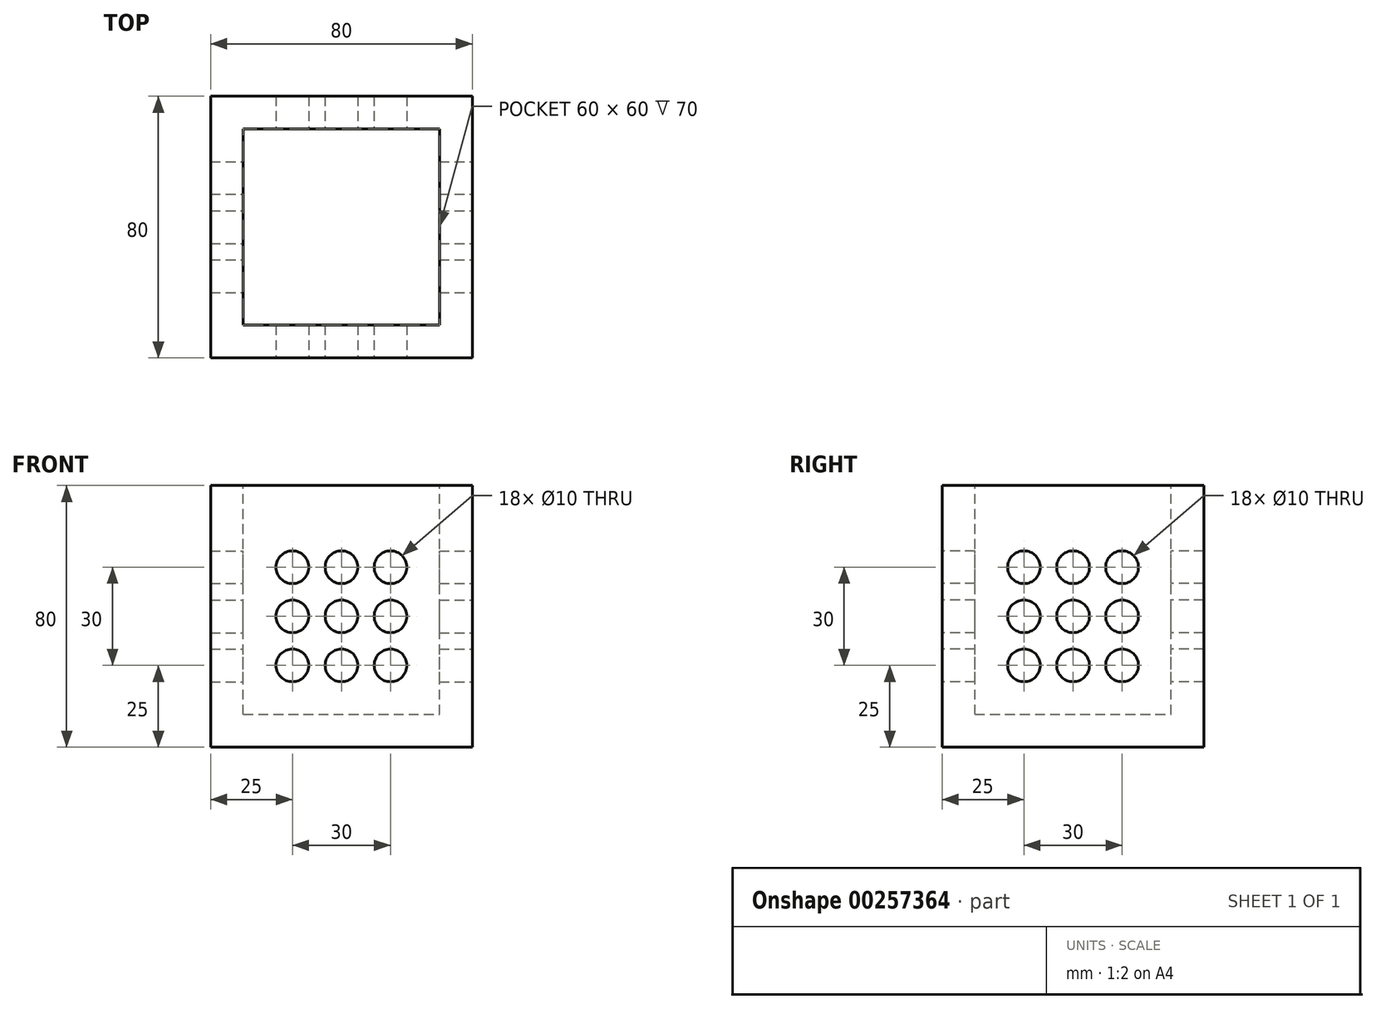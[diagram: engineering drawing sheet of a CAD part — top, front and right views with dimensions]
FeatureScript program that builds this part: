
annotation { "Feature Type Name" : "Feature", "Feature Type Description" : "" }
export const myFeature = defineFeature(function(context is Context, id is Id, definition is map)
    precondition{}
    {
        {
            var Q0;
            Q0=qCreatedBy(makeId("Front.planeOp"),FACE);
            var sketch = newSketch(context, id + "F0", { "sketchPlane" : qUnion([Q0])});
            skLineSegment(sketch, "E0.bottom", {"start": v(0, 0) * mm, "end": v(80, 0) * mm});
            skLineSegment(sketch, "E0.top", {"start": v(0, 80) * mm, "end": v(80, 80) * mm});
            skLineSegment(sketch, "E0.left", {"start": v(0, 0) * mm, "end": v(0, 80) * mm});
            skLineSegment(sketch, "E0.right", {"start": v(80, 0) * mm, "end": v(80, 80) * mm});
            skSolve(sketch);
        }
        {
            var Q0;
            Q0=makeQuery(id+"F0.imprint","IMPRINT",FACE,{"disambiguationData":[TD([[makeQuery(id+"F0.imprint","IMPRINT",EDGE,{"derivedFrom":sQuery(id+"F0.wireOp",EDGE,"E0.bottom")}),1.0]])]});
            extrude(context, id + "F1", {"entities" : qUnion([Q0]), "depth" : 80 * mm});
        }
        {
            var Q0;
            Q0=makeQuery(id+"F1.opExtrude","SWEPT_FACE",FACE,{"disambiguationData":[OSD([sQuery(id+"F0.wireOp",EDGE,"E0.top")])]});
            var sketch = newSketch(context, id + "F2", { "sketchPlane" : qUnion([Q0])});
            skLineSegment(sketch, "E1.bottom", {"start": v(10, -70) * mm, "end": v(70, -70) * mm});
            skLineSegment(sketch, "E1.top", {"start": v(10, -10) * mm, "end": v(70, -10) * mm});
            skLineSegment(sketch, "E1.left", {"start": v(10, -70) * mm, "end": v(10, -10) * mm});
            skLineSegment(sketch, "E1.right", {"start": v(70, -70) * mm, "end": v(70, -10) * mm});
            skSolve(sketch);
        }
        {
            var Q0;
            Q0=makeQuery(id+"F2.imprint","IMPRINT",FACE,{"disambiguationData":[TD([[makeQuery(id+"F2.imprint","IMPRINT",EDGE,{"derivedFrom":sQuery(id+"F2.wireOp",EDGE,"E1.bottom")}),1.0]])]});
            extrude(context, id + "F3", {"entities" : qUnion([Q0]), "operationType" : NewBodyOperationType.REMOVE, "oppositeDirection" : true, "depth" : 70 * mm});
        }
        {
            var Q0;
            Q0=makeQuery(id+"F1.opExtrude","CAP_FACE",FACE,{"disambiguationData":[OSD([sQuery(id+"F0.wireOp",EDGE,"E0.bottom"),sQuery(id+"F0.wireOp",EDGE,"E0.top"),sQuery(id+"F0.wireOp",EDGE,"E0.left"),sQuery(id+"F0.wireOp",EDGE,"E0.right")])],"isStart":false});
            var sketch = newSketch(context, id + "F4", { "sketchPlane" : qUnion([Q0])});
            skLineSegment(sketch, "E2.bottom", {"start": v(10, 10) * mm, "end": v(70, 10) * mm});
            skLineSegment(sketch, "E2.top", {"start": v(10, 70) * mm, "end": v(70, 70) * mm});
            skLineSegment(sketch, "E2.left", {"start": v(10, 10) * mm, "end": v(10, 70) * mm});
            skLineSegment(sketch, "E2.right", {"start": v(70, 10) * mm, "end": v(70, 70) * mm});
            skLineSegment(sketch, "E3", {"start": v(25, 10) * mm, "end": v(25, 20) * mm});
            skLineSegment(sketch, "E4", {"start": v(40, 10) * mm, "end": v(40, 20) * mm});
            skLineSegment(sketch, "E5", {"start": v(55, 10) * mm, "end": v(55, 20) * mm});
            skLineSegment(sketch, "E6", {"start": v(10, 55) * mm, "end": v(20, 55) * mm});
            skLineSegment(sketch, "E7", {"start": v(10, 40) * mm, "end": v(20, 40) * mm});
            skLineSegment(sketch, "E8", {"start": v(10, 25) * mm, "end": v(20, 25) * mm});
            skCircle(sketch, "E9", {"center": v(25, 55) * mm, "radius": 5 * mm});
            skCircle(sketch, "E10", {"center": v(40, 55) * mm, "radius": 5 * mm});
            skCircle(sketch, "E11", {"center": v(55, 55) * mm, "radius": 5 * mm});
            skCircle(sketch, "E12", {"center": v(55, 40) * mm, "radius": 5 * mm});
            skCircle(sketch, "E13", {"center": v(40, 40) * mm, "radius": 5 * mm});
            skCircle(sketch, "E14", {"center": v(25, 40) * mm, "radius": 5 * mm});
            skCircle(sketch, "E15", {"center": v(25, 25) * mm, "radius": 5 * mm});
            skCircle(sketch, "E16", {"center": v(40, 25) * mm, "radius": 5 * mm});
            skCircle(sketch, "E17", {"center": v(55, 25) * mm, "radius": 5 * mm});
            skLineSegment(sketch, "E18.trimOffspring", {"start": v(25, 60) * mm, "end": v(25, 70) * mm});
            skLineSegment(sketch, "E19.trimOffspring", {"start": v(30, 55) * mm, "end": v(35, 55) * mm});
            skLineSegment(sketch, "E20.trimOffspring", {"start": v(45, 55) * mm, "end": v(50, 55) * mm});
            skLineSegment(sketch, "E21.trimOffspring", {"start": v(40, 60) * mm, "end": v(40, 70) * mm});
            skLineSegment(sketch, "E22.trimOffspring", {"start": v(60, 55) * mm, "end": v(70, 55) * mm});
            skLineSegment(sketch, "E23.trimOffspring", {"start": v(55, 60) * mm, "end": v(55, 70) * mm});
            skLineSegment(sketch, "E24.trimOffspring", {"start": v(25, 45) * mm, "end": v(25, 50) * mm});
            skLineSegment(sketch, "E25.trimOffspring", {"start": v(30, 40) * mm, "end": v(35, 40) * mm});
            skLineSegment(sketch, "E26.trimOffspring", {"start": v(45, 40) * mm, "end": v(50, 40) * mm});
            skLineSegment(sketch, "E27.trimOffspring", {"start": v(40, 45) * mm, "end": v(40, 50) * mm});
            skLineSegment(sketch, "E28.trimOffspring", {"start": v(60, 40) * mm, "end": v(70, 40) * mm});
            skLineSegment(sketch, "E29.trimOffspring", {"start": v(55, 45) * mm, "end": v(55, 50) * mm});
            skLineSegment(sketch, "E30.trimOffspring", {"start": v(25, 30) * mm, "end": v(25, 35) * mm});
            skLineSegment(sketch, "E31.trimOffspring", {"start": v(30, 25) * mm, "end": v(35, 25) * mm});
            skLineSegment(sketch, "E32.trimOffspring", {"start": v(45, 25) * mm, "end": v(50, 25) * mm});
            skLineSegment(sketch, "E33.trimOffspring", {"start": v(40, 30) * mm, "end": v(40, 35) * mm});
            skLineSegment(sketch, "E34.trimOffspring", {"start": v(60, 25) * mm, "end": v(70, 25) * mm});
            skLineSegment(sketch, "E35.trimOffspring", {"start": v(55, 30) * mm, "end": v(55, 35) * mm});
            skSolve(sketch);
        }
        {
            var Q0;
            Q0=makeQuery(id+"F1.opExtrude","SWEPT_FACE",FACE,{"disambiguationData":[OSD([sQuery(id+"F0.wireOp",EDGE,"E0.right")])]});
            var sketch = newSketch(context, id + "F5", { "sketchPlane" : qUnion([Q0])});
            skLineSegment(sketch, "E36.bottom", {"start": v(-70, 10) * mm, "end": v(-10, 10) * mm});
            skLineSegment(sketch, "E36.top", {"start": v(-70, 70) * mm, "end": v(-10, 70) * mm});
            skLineSegment(sketch, "E36.left", {"start": v(-70, 10) * mm, "end": v(-70, 70) * mm});
            skLineSegment(sketch, "E36.right", {"start": v(-10, 10) * mm, "end": v(-10, 70) * mm});
            skLineSegment(sketch, "E37", {"start": v(-55, 10) * mm, "end": v(-55, 20) * mm});
            skLineSegment(sketch, "E38", {"start": v(-40, 10) * mm, "end": v(-40, 20) * mm});
            skLineSegment(sketch, "E39", {"start": v(-25, 10) * mm, "end": v(-25, 20) * mm});
            skLineSegment(sketch, "E40", {"start": v(-70, 55) * mm, "end": v(-60, 55) * mm});
            skLineSegment(sketch, "E41", {"start": v(-70, 40) * mm, "end": v(-60, 40) * mm});
            skLineSegment(sketch, "E42", {"start": v(-70, 25) * mm, "end": v(-60, 25) * mm});
            skCircle(sketch, "E43", {"center": v(-55, 55) * mm, "radius": 5 * mm});
            skCircle(sketch, "E44", {"center": v(-40, 55) * mm, "radius": 5 * mm});
            skCircle(sketch, "E45", {"center": v(-25, 55) * mm, "radius": 5 * mm});
            skCircle(sketch, "E46", {"center": v(-25, 40) * mm, "radius": 5 * mm});
            skCircle(sketch, "E47", {"center": v(-40, 40) * mm, "radius": 5 * mm});
            skCircle(sketch, "E48", {"center": v(-55, 40) * mm, "radius": 5 * mm});
            skCircle(sketch, "E49", {"center": v(-55, 25) * mm, "radius": 5 * mm});
            skCircle(sketch, "E50", {"center": v(-40, 25) * mm, "radius": 5 * mm});
            skCircle(sketch, "E51", {"center": v(-25, 25) * mm, "radius": 5 * mm});
            skLineSegment(sketch, "E52.trimOffspring", {"start": v(-55, 60) * mm, "end": v(-55, 70) * mm});
            skLineSegment(sketch, "E53.trimOffspring", {"start": v(-50, 55) * mm, "end": v(-45, 55) * mm});
            skLineSegment(sketch, "E54.trimOffspring", {"start": v(-35, 55) * mm, "end": v(-30, 55) * mm});
            skLineSegment(sketch, "E55.trimOffspring", {"start": v(-40, 60) * mm, "end": v(-40, 70) * mm});
            skLineSegment(sketch, "E56.trimOffspring", {"start": v(-20, 55) * mm, "end": v(-10, 55) * mm});
            skLineSegment(sketch, "E57.trimOffspring", {"start": v(-25, 60) * mm, "end": v(-25, 70) * mm});
            skLineSegment(sketch, "E58.trimOffspring", {"start": v(-55, 45) * mm, "end": v(-55, 50) * mm});
            skLineSegment(sketch, "E59.trimOffspring", {"start": v(-50, 40) * mm, "end": v(-45, 40) * mm});
            skLineSegment(sketch, "E60.trimOffspring", {"start": v(-35, 40) * mm, "end": v(-30, 40) * mm});
            skLineSegment(sketch, "E61.trimOffspring", {"start": v(-40, 45) * mm, "end": v(-40, 50) * mm});
            skLineSegment(sketch, "E62.trimOffspring", {"start": v(-20, 40) * mm, "end": v(-10, 40) * mm});
            skLineSegment(sketch, "E63.trimOffspring", {"start": v(-25, 45) * mm, "end": v(-25, 50) * mm});
            skLineSegment(sketch, "E64.trimOffspring", {"start": v(-55, 30) * mm, "end": v(-55, 35) * mm});
            skLineSegment(sketch, "E65.trimOffspring", {"start": v(-50, 25) * mm, "end": v(-45, 25) * mm});
            skLineSegment(sketch, "E66.trimOffspring", {"start": v(-35, 25) * mm, "end": v(-30, 25) * mm});
            skLineSegment(sketch, "E67.trimOffspring", {"start": v(-40, 30) * mm, "end": v(-40, 35) * mm});
            skLineSegment(sketch, "E68.trimOffspring", {"start": v(-20, 25) * mm, "end": v(-10, 25) * mm});
            skLineSegment(sketch, "E69.trimOffspring", {"start": v(-25, 30) * mm, "end": v(-25, 35) * mm});
            skSolve(sketch);
        }
        {
            var Q0;
            {var subQ0=sQuery(id+"F4.wireOp",EDGE,"E9");var subQ1=makeQuery(id+"F4.imprint","INTERSECT",VERTEX,{"derivedFrom":[subQ0,sQuery(id+"F4.wireOp",EDGE,"E18.trimOffspring")]});Q0=makeQuery(id+"F4.imprint","IMPRINT",FACE,{"disambiguationData":[TD([[makeQuery(id+"F4.imprint","IMPRINT",EDGE,{"disambiguationData":[TD([[subQ1,1.0]])],"derivedFrom":subQ0}),1.0]])]});}
            var Q1;
            {var subQ0=sQuery(id+"F4.wireOp",EDGE,"E10");var subQ1=makeQuery(id+"F4.imprint","INTERSECT",VERTEX,{"derivedFrom":[subQ0,sQuery(id+"F4.wireOp",EDGE,"E20.trimOffspring")]});Q1=makeQuery(id+"F4.imprint","IMPRINT",FACE,{"disambiguationData":[TD([[makeQuery(id+"F4.imprint","IMPRINT",EDGE,{"disambiguationData":[TD([[subQ1,-1.0]])],"derivedFrom":subQ0}),1.0]])]});}
            var Q2;
            {var subQ0=sQuery(id+"F4.wireOp",EDGE,"E11");var subQ1=makeQuery(id+"F4.imprint","INTERSECT",VERTEX,{"derivedFrom":[subQ0,sQuery(id+"F4.wireOp",EDGE,"E22.trimOffspring")]});Q2=makeQuery(id+"F4.imprint","IMPRINT",FACE,{"disambiguationData":[TD([[makeQuery(id+"F4.imprint","IMPRINT",EDGE,{"disambiguationData":[TD([[subQ1,-1.0]])],"derivedFrom":subQ0}),1.0]])]});}
            var Q3;
            {var subQ0=sQuery(id+"F4.wireOp",EDGE,"E12");var subQ1=makeQuery(id+"F4.imprint","INTERSECT",VERTEX,{"derivedFrom":[subQ0,sQuery(id+"F4.wireOp",EDGE,"E28.trimOffspring")]});Q3=makeQuery(id+"F4.imprint","IMPRINT",FACE,{"disambiguationData":[TD([[makeQuery(id+"F4.imprint","IMPRINT",EDGE,{"disambiguationData":[TD([[subQ1,-1.0]])],"derivedFrom":subQ0}),1.0]])]});}
            var Q4;
            {var subQ0=sQuery(id+"F4.wireOp",EDGE,"E17");var subQ1=makeQuery(id+"F4.imprint","INTERSECT",VERTEX,{"derivedFrom":[subQ0,sQuery(id+"F4.wireOp",EDGE,"E34.trimOffspring")]});Q4=makeQuery(id+"F4.imprint","IMPRINT",FACE,{"disambiguationData":[TD([[makeQuery(id+"F4.imprint","IMPRINT",EDGE,{"disambiguationData":[TD([[subQ1,-1.0]])],"derivedFrom":subQ0}),1.0]])]});}
            var Q5;
            {var subQ0=sQuery(id+"F4.wireOp",EDGE,"E16");var subQ1=makeQuery(id+"F4.imprint","INTERSECT",VERTEX,{"derivedFrom":[subQ0,sQuery(id+"F4.wireOp",EDGE,"E32.trimOffspring")]});Q5=makeQuery(id+"F4.imprint","IMPRINT",FACE,{"disambiguationData":[TD([[makeQuery(id+"F4.imprint","IMPRINT",EDGE,{"disambiguationData":[TD([[subQ1,-1.0]])],"derivedFrom":subQ0}),1.0]])]});}
            var Q6;
            {var subQ0=sQuery(id+"F4.wireOp",EDGE,"E13");var subQ1=makeQuery(id+"F4.imprint","INTERSECT",VERTEX,{"derivedFrom":[subQ0,sQuery(id+"F4.wireOp",EDGE,"E26.trimOffspring")]});Q6=makeQuery(id+"F4.imprint","IMPRINT",FACE,{"disambiguationData":[TD([[makeQuery(id+"F4.imprint","IMPRINT",EDGE,{"disambiguationData":[TD([[subQ1,-1.0]])],"derivedFrom":subQ0}),1.0]])]});}
            var Q7;
            {var subQ0=sQuery(id+"F4.wireOp",EDGE,"E14");var subQ1=makeQuery(id+"F4.imprint","INTERSECT",VERTEX,{"derivedFrom":[subQ0,sQuery(id+"F4.wireOp",EDGE,"E24.trimOffspring")]});Q7=makeQuery(id+"F4.imprint","IMPRINT",FACE,{"disambiguationData":[TD([[makeQuery(id+"F4.imprint","IMPRINT",EDGE,{"disambiguationData":[TD([[subQ1,1.0]])],"derivedFrom":subQ0}),1.0]])]});}
            var Q8;
            {var subQ0=sQuery(id+"F4.wireOp",EDGE,"E15");var subQ1=makeQuery(id+"F4.imprint","INTERSECT",VERTEX,{"derivedFrom":[subQ0,sQuery(id+"F4.wireOp",EDGE,"E30.trimOffspring")]});Q8=makeQuery(id+"F4.imprint","IMPRINT",FACE,{"disambiguationData":[TD([[makeQuery(id+"F4.imprint","IMPRINT",EDGE,{"disambiguationData":[TD([[subQ1,1.0]])],"derivedFrom":subQ0}),1.0]])]});}
            extrude(context, id + "F6", {"entities" : qUnion([Q0, Q1, Q2, Q3, Q4, Q5, Q6, Q7, Q8]), "operationType" : NewBodyOperationType.REMOVE, "oppositeDirection" : true, "depth" : 254 * mm});
        }
        {
            var Q0;
            {var subQ0=sQuery(id+"F5.wireOp",EDGE,"E43");var subQ1=makeQuery(id+"F5.imprint","INTERSECT",VERTEX,{"derivedFrom":[subQ0,sQuery(id+"F5.wireOp",EDGE,"E52.trimOffspring")]});Q0=makeQuery(id+"F5.imprint","IMPRINT",FACE,{"disambiguationData":[TD([[makeQuery(id+"F5.imprint","IMPRINT",EDGE,{"disambiguationData":[TD([[subQ1,1.0]])],"derivedFrom":subQ0}),1.0]])]});}
            var Q1;
            {var subQ0=sQuery(id+"F5.wireOp",EDGE,"E44");var subQ1=makeQuery(id+"F5.imprint","INTERSECT",VERTEX,{"derivedFrom":[subQ0,sQuery(id+"F5.wireOp",EDGE,"E54.trimOffspring")]});Q1=makeQuery(id+"F5.imprint","IMPRINT",FACE,{"disambiguationData":[TD([[makeQuery(id+"F5.imprint","IMPRINT",EDGE,{"disambiguationData":[TD([[subQ1,-1.0]])],"derivedFrom":subQ0}),1.0]])]});}
            var Q2;
            {var subQ0=sQuery(id+"F5.wireOp",EDGE,"E45");var subQ1=makeQuery(id+"F5.imprint","INTERSECT",VERTEX,{"derivedFrom":[subQ0,sQuery(id+"F5.wireOp",EDGE,"E56.trimOffspring")]});Q2=makeQuery(id+"F5.imprint","IMPRINT",FACE,{"disambiguationData":[TD([[makeQuery(id+"F5.imprint","IMPRINT",EDGE,{"disambiguationData":[TD([[subQ1,-1.0]])],"derivedFrom":subQ0}),1.0]])]});}
            var Q3;
            {var subQ0=sQuery(id+"F5.wireOp",EDGE,"E46");var subQ1=makeQuery(id+"F5.imprint","INTERSECT",VERTEX,{"derivedFrom":[subQ0,sQuery(id+"F5.wireOp",EDGE,"E62.trimOffspring")]});Q3=makeQuery(id+"F5.imprint","IMPRINT",FACE,{"disambiguationData":[TD([[makeQuery(id+"F5.imprint","IMPRINT",EDGE,{"disambiguationData":[TD([[subQ1,-1.0]])],"derivedFrom":subQ0}),1.0]])]});}
            var Q4;
            {var subQ0=sQuery(id+"F5.wireOp",EDGE,"E51");var subQ1=makeQuery(id+"F5.imprint","INTERSECT",VERTEX,{"derivedFrom":[subQ0,sQuery(id+"F5.wireOp",EDGE,"E68.trimOffspring")]});Q4=makeQuery(id+"F5.imprint","IMPRINT",FACE,{"disambiguationData":[TD([[makeQuery(id+"F5.imprint","IMPRINT",EDGE,{"disambiguationData":[TD([[subQ1,-1.0]])],"derivedFrom":subQ0}),1.0]])]});}
            var Q5;
            {var subQ0=sQuery(id+"F5.wireOp",EDGE,"E50");var subQ1=makeQuery(id+"F5.imprint","INTERSECT",VERTEX,{"derivedFrom":[subQ0,sQuery(id+"F5.wireOp",EDGE,"E66.trimOffspring")]});Q5=makeQuery(id+"F5.imprint","IMPRINT",FACE,{"disambiguationData":[TD([[makeQuery(id+"F5.imprint","IMPRINT",EDGE,{"disambiguationData":[TD([[subQ1,-1.0]])],"derivedFrom":subQ0}),1.0]])]});}
            var Q6;
            {var subQ0=sQuery(id+"F5.wireOp",EDGE,"E49");var subQ1=makeQuery(id+"F5.imprint","INTERSECT",VERTEX,{"derivedFrom":[subQ0,sQuery(id+"F5.wireOp",EDGE,"E64.trimOffspring")]});Q6=makeQuery(id+"F5.imprint","IMPRINT",FACE,{"disambiguationData":[TD([[makeQuery(id+"F5.imprint","IMPRINT",EDGE,{"disambiguationData":[TD([[subQ1,1.0]])],"derivedFrom":subQ0}),1.0]])]});}
            var Q7;
            {var subQ0=sQuery(id+"F5.wireOp",EDGE,"E48");var subQ1=makeQuery(id+"F5.imprint","INTERSECT",VERTEX,{"derivedFrom":[subQ0,sQuery(id+"F5.wireOp",EDGE,"E58.trimOffspring")]});Q7=makeQuery(id+"F5.imprint","IMPRINT",FACE,{"disambiguationData":[TD([[makeQuery(id+"F5.imprint","IMPRINT",EDGE,{"disambiguationData":[TD([[subQ1,1.0]])],"derivedFrom":subQ0}),1.0]])]});}
            var Q8;
            {var subQ0=sQuery(id+"F5.wireOp",EDGE,"E47");var subQ1=makeQuery(id+"F5.imprint","INTERSECT",VERTEX,{"derivedFrom":[subQ0,sQuery(id+"F5.wireOp",EDGE,"E60.trimOffspring")]});Q8=makeQuery(id+"F5.imprint","IMPRINT",FACE,{"disambiguationData":[TD([[makeQuery(id+"F5.imprint","IMPRINT",EDGE,{"disambiguationData":[TD([[subQ1,-1.0]])],"derivedFrom":subQ0}),1.0]])]});}
            extrude(context, id + "F7", {"entities" : qUnion([Q0, Q1, Q2, Q3, Q4, Q5, Q6, Q7, Q8]), "operationType" : NewBodyOperationType.REMOVE, "oppositeDirection" : true, "depth" : 254 * mm});
        }
    });
